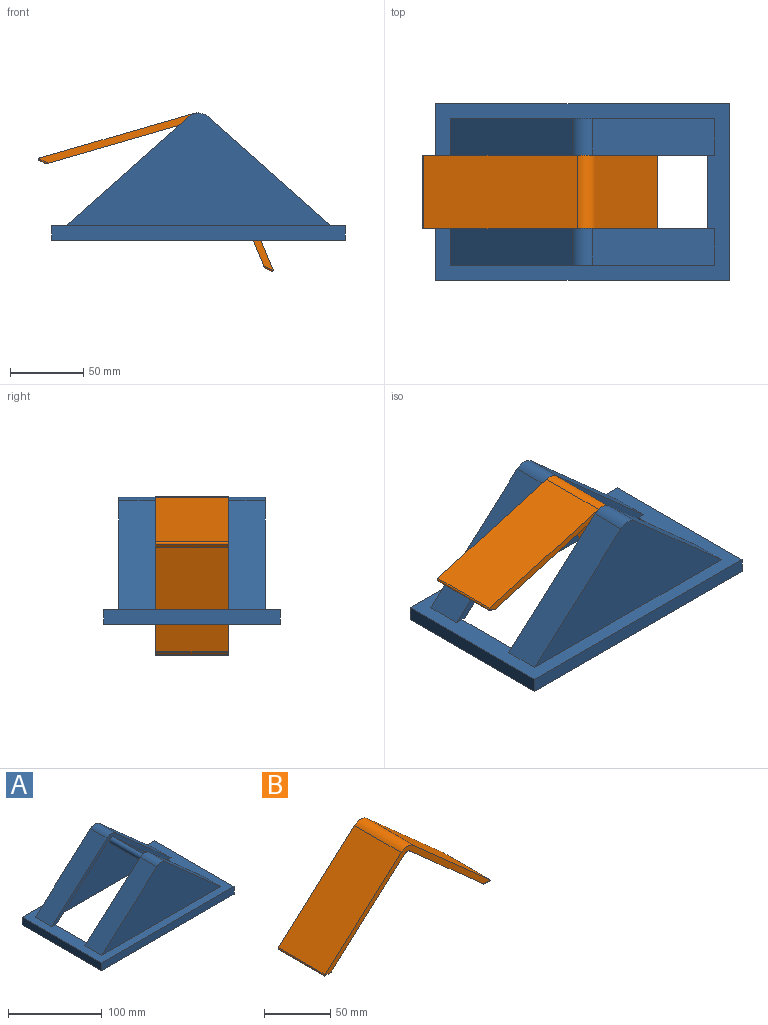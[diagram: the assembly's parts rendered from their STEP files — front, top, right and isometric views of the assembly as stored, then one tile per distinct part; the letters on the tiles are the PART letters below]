
ASSEMBLY  parts=2 mates=1
PART A: 33 faces, bbox 200x120x86.6 mm
  f0: plane 20x2.53mm, normal (0,0,-1), area 50.5mm2, adj f3,f5,f10,f30
  f1: plane 20x2.53mm, normal (0,0,-1), area 50.5mm2, adj f3,f5,f9,f29
  f2: plane 20x2.53mm, normal (0,0,-1), area 50.5mm2, adj f15,f21,f23,f29
  f3: plane 180x76.62mm, normal (0,-1,0), area 1139.7mm2, adj f0,f1,f6,f7,f8,f9,f10,f11
  f4: plane 180x76.62mm, normal (0,1,0), area 7183.8mm2, adj f6,f7,f8,f25
  f5: plane 170x81.62mm, normal (0,-1,0), area 7742.1mm2, adj f0,f1,f9,f10,f11,f29,f30,f32
  f6: plane 83.36x74.09mm, normal (0.66,0,0.75), area 2788.2mm2, adj f3,f4,f8,f25
  f7: plane 83.36x74.09mm, normal (-0.66,0,0.75), area 2788.2mm2, adj f3,f4,f8,f25
  f8: cylinder r=10mm len=25mm, axis (0,-1,0), area 363.3mm2, adj f3,f4,f6,f7
  f9: plane 79.15x70.36mm, normal (-0.66,0,-0.75), area 2118mm2, adj f1,f3,f5,f11
  f10: plane 79.15x70.36mm, normal (0.66,0,-0.75), area 2118mm2, adj f0,f3,f5,f11
  f11: cylinder r=5mm len=20mm, axis (0,-1,0), area 145.3mm2, adj f3,f5,f9,f10,f12
  f12: plane 7.22x6.75mm, normal (0,1,0), area 39.1mm2, adj f11,f14
  f13: plane 7.22x6.75mm, normal (0,-1,0), area 39.1mm2, adj f14,f24
  f14: cylinder r=3.61mm len=50mm, axis (0,1,0), area 1134.6mm2, adj f3,f12,f13,f15
  f15: plane 180x76.62mm, normal (0,1,0), area 1139.7mm2, adj f2,f14,f16,f17,f18,f20,f21,f22
  f16: plane 20x2.53mm, normal (0,0,-1), area 50.5mm2, adj f15,f22,f23,f30
  f17: plane 83.36x74.09mm, normal (0.66,0,0.75), area 2788.2mm2, adj f15,f19,f20,f25
  f18: plane 83.36x74.09mm, normal (-0.66,0,0.75), area 2788.2mm2, adj f15,f19,f20,f25
  f19: plane 180x76.62mm, normal (0,-1,0), area 7183.8mm2, adj f17,f18,f20,f25
  f20: cylinder r=10mm len=25mm, axis (0,-1,0), area 363.3mm2, adj f15,f17,f18,f19
  f21: plane 79.15x70.36mm, normal (-0.66,0,-0.75), area 2118mm2, adj f2,f15,f23,f24
  f22: plane 79.15x70.36mm, normal (0.66,0,-0.75), area 2118mm2, adj f15,f16,f23,f24
  f23: plane 170x81.62mm, normal (0,1,0), area 7742.1mm2, adj f2,f16,f21,f22,f24,f29,f30,f32
  f24: cylinder r=5mm len=20mm, axis (0,-1,0), area 145.3mm2, adj f13,f15,f21,f22,f23
  f25: plane 200x120mm, normal (0,0,1), area 6500mm2, adj f3,f4,f6,f7,f15,f17,f18,f19
  f26: plane 120x10mm, normal (-1,0,0), area 1200mm2, adj f25,f27,f31,f32
  f27: plane 200x10mm, normal (0,1,0), area 2000mm2, adj f25,f26,f28,f32
  f28: plane 120x10mm, normal (1,0,0), area 1200mm2, adj f25,f27,f31,f32
  f29: plane 90x10mm, normal (-1,0,0), area 900mm2, adj f1,f2,f5,f23,f25,f32
  f30: plane 90x10mm, normal (1,0,0), area 900mm2, adj f0,f5,f16,f23,f25,f32
  f31: plane 200x10mm, normal (0,-1,0), area 2000mm2, adj f25,f26,f28,f32
  f32: plane 200x120mm, normal (0,0,-1), area 8700mm2, adj f5,f23,f26,f27,f28,f29,f30,f31
PART B: 20 faces, bbox 176.7x50x76.6 mm
  f0: plane 176.74x75.62mm, normal (0,-1,0), area 1124.4mm2, adj f1,f2,f5,f6,f7,f8,f9,f11
  f1: cylinder r=5mm len=50mm, axis (0,-1,0), area 33.5mm2, adj f0,f3,f5,f11
  f2: cylinder r=5mm len=50mm, axis (0,-1,0), area 33.5mm2, adj f0,f3,f6,f11
  f3: plane 176.74x75.62mm, normal (0,1,0), area 1124.4mm2, adj f1,f2,f5,f6,f7,f8,f9,f11
  f4: plane 48x4.52mm, normal (0,0,-1), area 216.7mm2, adj f16,f17,f18,f19
  f5: plane 78.87x70.11mm, normal (0.66,0,-0.75), area 5275.9mm2, adj f0,f1,f3,f12,f13,f15
  f6: plane 78.87x70.11mm, normal (-0.66,0,-0.75), area 5275.9mm2, adj f0,f2,f3,f16,f18,f19
  f7: cylinder r=10mm len=50mm, axis (0,-1,0), area 726.6mm2, adj f0,f3,f8,f9
  f8: plane 81.39x72.35mm, normal (-0.66,0,0.75), area 5444.8mm2, adj f0,f3,f7,f14
  f9: plane 81.39x72.35mm, normal (0.66,0,0.75), area 5444.8mm2, adj f0,f3,f7,f17
  f10: plane 48x4.52mm, normal (0,0,-1), area 216.7mm2, adj f12,f13,f14,f15
  f11: cylinder r=3.61mm len=50mm, axis (0,1,0), area 319.3mm2, adj f0,f1,f2,f3
  f12: cylinder r=1mm len=7.02mm, axis (-1,0,0), area 9.2mm2, adj f0,f5,f10,f13,f14
  f13: cylinder r=1mm len=49.33mm, axis (0,-1,0), area 35.4mm2, adj f5,f10,f12,f15
  f14: cylinder r=1mm len=50mm, axis (0,1,0), area 119.6mm2, adj f0,f3,f8,f10,f12,f15
  f15: cylinder r=1mm len=7.02mm, axis (1,0,0), area 9.2mm2, adj f3,f5,f10,f13,f14
  f16: cylinder r=1mm len=7.02mm, axis (-1,0,0), area 9.2mm2, adj f0,f4,f6,f17,f18
  f17: cylinder r=1mm len=50mm, axis (0,1,0), area 119.6mm2, adj f0,f3,f4,f9,f16,f19
  f18: cylinder r=1mm len=49.33mm, axis (0,-1,0), area 35.4mm2, adj f4,f6,f16,f19
  f19: cylinder r=1mm len=7.02mm, axis (1,0,0), area 9.2mm2, adj f3,f4,f6,f17,f18
PLACE A at identity fixed
PLACE B rot(axis=(0,1,0),25.5deg) t=(-29.44,0,6.65)mm
MATE revolute B.f11 <-> A.f14  axis (0,-1,0) through (0,25,68.48)mm
